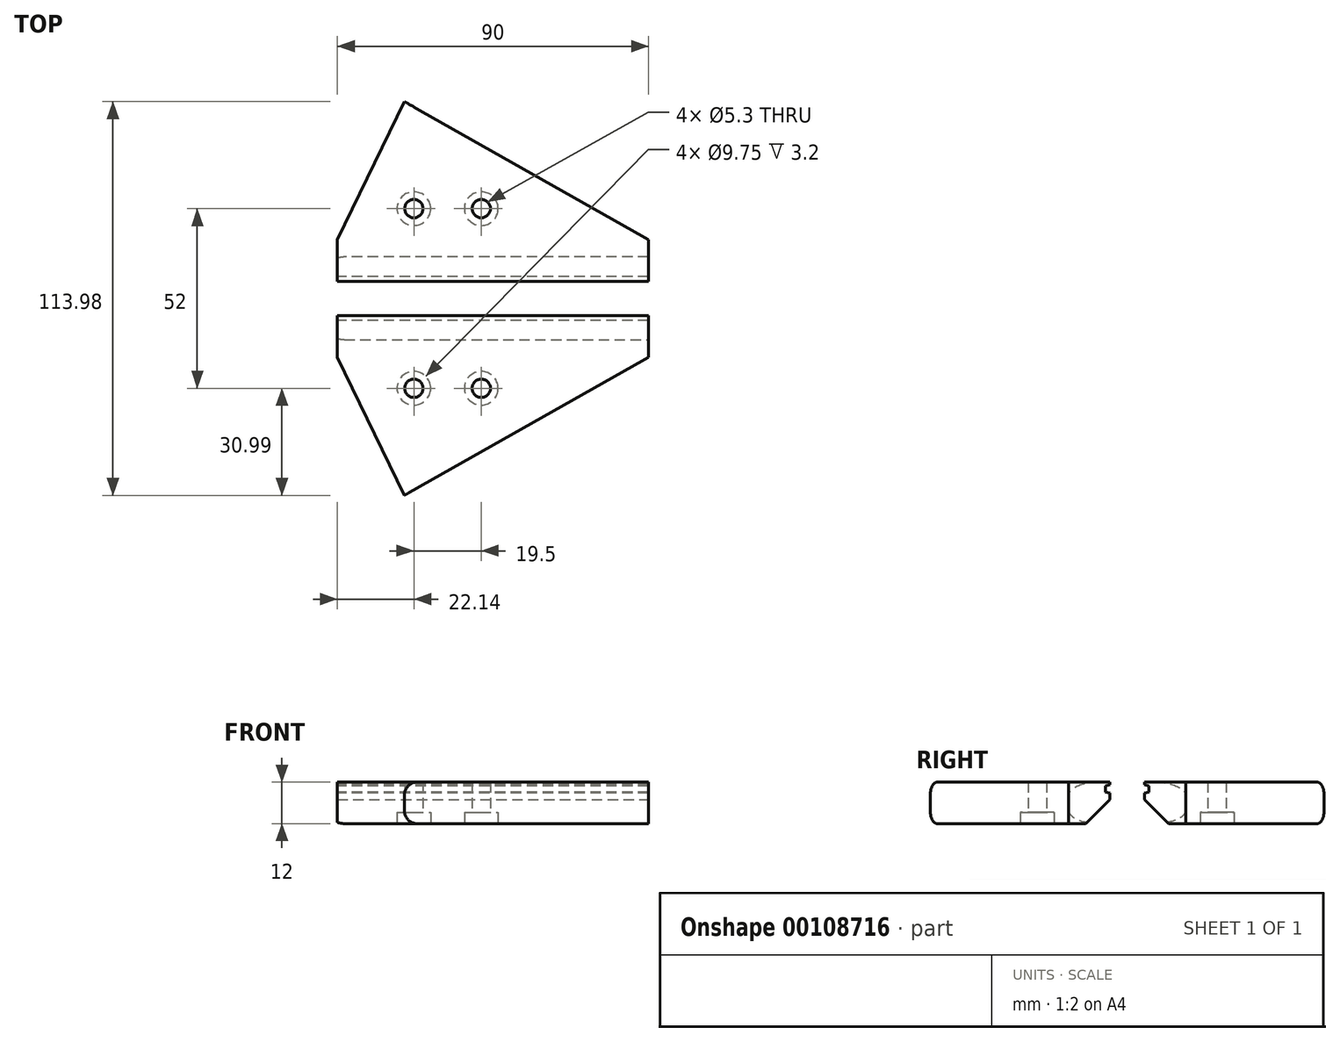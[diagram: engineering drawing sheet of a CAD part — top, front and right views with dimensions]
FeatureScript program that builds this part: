
annotation { "Feature Type Name" : "Feature", "Feature Type Description" : "" }
export const myFeature = defineFeature(function(context is Context, id is Id, definition is map)
    precondition{}
    {
        {
            var Q0;
            Q0=qCreatedBy(makeId("Top.planeOp"),FACE);
            var sketch = newSketch(context, id + "F0", { "sketchPlane" : qUnion([Q0])});
            skCircle(sketch, "E0", {"center": v(-9.75, -26) * mm, "radius": 4.75 * mm});
            skCircle(sketch, "E1", {"center": v(9.75, -26) * mm, "radius": 4.75 * mm});
            skCircle(sketch, "E2", {"center": v(-9.75, 26) * mm, "radius": 4.75 * mm});
            skCircle(sketch, "E3", {"center": v(9.75, 26) * mm, "radius": 4.75 * mm});
            skLineSegment(sketch, "E4", {"start": v(-9.75, 26) * mm, "end": v(9.75, 26) * mm, "construction": true});
            skPoint(sketch, "E5", {"position": v(0, 26) * mm});
            skLineSegment(sketch, "E6.bottom", {"start": v(19.1, 13.2) * mm, "end": v(-19.1, 13.2) * mm, "construction": true});
            skLineSegment(sketch, "E6.top", {"start": v(19.1, 38.8) * mm, "end": v(-19.1, 38.8) * mm, "construction": true});
            skLineSegment(sketch, "E6.left", {"start": v(19.1, 13.2) * mm, "end": v(19.1, 38.8) * mm, "construction": true});
            skLineSegment(sketch, "E6.right", {"start": v(-19.1, 13.2) * mm, "end": v(-19.1, 38.8) * mm, "construction": true});
            skLineSegment(sketch, "E7", {"start": v(-9.75, -26) * mm, "end": v(9.75, -26) * mm, "construction": true});
            skLineSegment(sketch, "E8", {"start": v(0, 26) * mm, "end": v(0, -26) * mm, "construction": true});
            skPoint(sketch, "E9", {"position": v(0, 0) * mm});
            skLineSegment(sketch, "E10.bottom", {"start": v(19.1, -38.8) * mm, "end": v(-19.1, -38.8) * mm, "construction": true});
            skLineSegment(sketch, "E10.top", {"start": v(19.1, -13.2) * mm, "end": v(-19.1, -13.2) * mm, "construction": true});
            skLineSegment(sketch, "E10.left", {"start": v(19.1, -38.8) * mm, "end": v(19.1, -13.2) * mm, "construction": true});
            skLineSegment(sketch, "E10.right", {"start": v(-19.1, -38.8) * mm, "end": v(-19.1, -13.2) * mm, "construction": true});
            skPoint(sketch, "E10.middle", {"position": v(0, -26) * mm});
            skSolve(sketch);
        }
        {
            var Q0;
            Q0=qCreatedBy(makeId("Top.planeOp"),FACE);
            var sketch = newSketch(context, id + "F1", { "sketchPlane" : qUnion([Q0])});
            skLineSegment(sketch, "E11", {"start": v(-31.9, 5) * mm, "end": v(58.1, 5) * mm});
            skLineSegment(sketch, "E12", {"start": v(-31.9, 5) * mm, "end": v(-31.9, 17) * mm});
            skLineSegment(sketch, "E13", {"start": v(58.1, 5) * mm, "end": v(58.1, 17) * mm});
            skLineSegment(sketch, "E14", {"start": v(58.1, 17) * mm, "end": v(-12.5, 57) * mm});
            skLineSegment(sketch, "E15", {"start": v(-31.9, 17) * mm, "end": v(-12.5, 57) * mm});
            skPoint(sketch, "E16", {"position": v(-9.75, 26) * mm});
            skPoint(sketch, "E17", {"position": v(9.75, 26) * mm});
            skLineSegment(sketch, "E18", {"start": v(-12.5, 57) * mm, "end": v(-47.57, 76.85) * mm, "construction": true});
            skLineSegment(sketch, "E19", {"start": v(-9.75, 26) * mm, "end": v(-24.15, 32.98) * mm, "construction": true});
            skLineSegment(sketch, "E20", {"start": v(9.75, 26) * mm, "end": v(17.64, 39.92) * mm, "construction": true});
            skLineSegment(sketch, "E21.MirrorCS", {"start": v(58.1, -17) * mm, "end": v(-12.5, -57) * mm, "construction": true});
            skLineSegment(sketch, "E22.MirrorCS", {"start": v(-31.9, -17) * mm, "end": v(-12.5, -57) * mm, "construction": true});
            skLineSegment(sketch, "E23.MirrorCS", {"start": v(58.1, -5) * mm, "end": v(58.1, -17) * mm});
            skLineSegment(sketch, "E24.MirrorCS", {"start": v(-31.9, -5) * mm, "end": v(-31.9, -17) * mm});
            skLineSegment(sketch, "E25.MirrorCS", {"start": v(58.1, -17) * mm, "end": v(-12.5, -57) * mm});
            skLineSegment(sketch, "E26.MirrorCS", {"start": v(-9.75, -26) * mm, "end": v(-24.15, -32.98) * mm, "construction": true});
            skPoint(sketch, "E27.MirrorP", {"position": v(-9.75, -26) * mm});
            skLineSegment(sketch, "E28.MirrorCS", {"start": v(9.75, -26) * mm, "end": v(17.64, -39.92) * mm, "construction": true});
            skPoint(sketch, "E29.MirrorP", {"position": v(9.75, -26) * mm});
            skLineSegment(sketch, "E30.MirrorCS", {"start": v(-31.9, -5) * mm, "end": v(58.1, -5) * mm});
            skLineSegment(sketch, "E31.MirrorCS", {"start": v(-31.9, -17) * mm, "end": v(-12.5, -57) * mm});
            skLineSegment(sketch, "E32.MirrorCS", {"start": v(58.1, 17) * mm, "end": v(-12.5, 57) * mm, "construction": true});
            skLineSegment(sketch, "E33.MirrorCS", {"start": v(-31.9, 17) * mm, "end": v(-12.5, 57) * mm, "construction": true});
            skSolve(sketch);
        }
        {
            var Q0;
            Q0=makeQuery(id+"F1.imprint","IMPRINT",FACE,{"disambiguationData":[TD([[makeQuery(id+"F1.imprint","IMPRINT",EDGE,{"derivedFrom":sQuery(id+"F1.wireOp",EDGE,"E11")}),1.0]])]});
            var Q1;
            Q1=makeQuery(id+"F1.imprint","IMPRINT",FACE,{"disambiguationData":[TD([[makeQuery(id+"F1.imprint","IMPRINT",EDGE,{"derivedFrom":sQuery(id+"F1.wireOp",EDGE,"f0b5c845-2ff2-45c4-aac1-717edb82d91d0.MirrorCS")}),1.0]])]});
            var Q2;
            Q2=makeQuery(id+"F1.imprint","IMPRINT",FACE,{"disambiguationData":[TD([[makeQuery(id+"F1.imprint","IMPRINT",EDGE,{"derivedFrom":sQuery(id+"F1.wireOp",EDGE,"E23.MirrorCS")}),-1.0]])]});
            extrude(context, id + "F2", {"entities" : qUnion([Q0, Q1, Q2]), "depth" : 12 * mm});
        }
        {
            var Q0;
            Q0=sQuery(id+"F0.wireOp",VERTEX,"E2.center");
            var Q1;
            Q1=sQuery(id+"F0.wireOp",VERTEX,"E3.center");
            var Q2;
            Q2=sQuery(id+"F0.wireOp",VERTEX,"E0.center");
            var Q3;
            Q3=sQuery(id+"F0.wireOp",VERTEX,"E1.center");
            var Q4;
            Q4=makeQuery(id+"F2.opExtrude","SWEPT_BODY",BODY,{"disambiguationData":[OSD([sQuery(id+"F1.wireOp",EDGE,"E11"),sQuery(id+"F1.wireOp",EDGE,"E12"),sQuery(id+"F1.wireOp",EDGE,"E13"),sQuery(id+"F1.wireOp",EDGE,"E14"),sQuery(id+"F1.wireOp",EDGE,"E15"),sQuery(id+"F1.wireOp",EDGE,"TzhvLS3T-Hups-Q3Qz-4XNe-3sz2j3HgjUnV")])]});
            var Q5;
            Q5=makeQuery(id+"F2.opExtrude","SWEPT_BODY",BODY,{"disambiguationData":[OSD([sQuery(id+"F1.wireOp",EDGE,"E23.MirrorCS"),sQuery(id+"F1.wireOp",EDGE,"E24.MirrorCS"),sQuery(id+"F1.wireOp",EDGE,"E25.MirrorCS"),sQuery(id+"F1.wireOp",EDGE,"E30.MirrorCS"),sQuery(id+"F1.wireOp",EDGE,"E31.MirrorCS")])]});
            hole(context, id + "F3", {"style" : HoleStyle.C_BORE, "endStyle" : HoleEndStyle.THROUGH, "oppositeDirection" : true, "holeDiameter" : 5.3 * mm, "cBoreDiameter" : 9.75 * mm, "cBoreDepth" : 3.2 * mm, "startFromSketch" : true, "locations" : qUnion([Q0, Q1, Q2, Q3]), "scope" : qUnion([Q4, Q5]), "isTappedThrough" : true});
        }
        {
            var Q0;
            Q0=qCreatedBy(makeId("Right.planeOp"),FACE);
            var sketch = newSketch(context, id + "F4", { "sketchPlane" : qUnion([Q0])});
            skLineSegment(sketch, "E34", {"start": v(6.3, 10.9) * mm, "end": v(6.3, 9.1) * mm});
            skPoint(sketch, "E35", {"position": v(5, 11.2) * mm});
            skLineSegment(sketch, "E36", {"start": v(5, 11.2) * mm, "end": v(6.3, 10.9) * mm});
            skLineSegment(sketch, "E37", {"start": v(6.3, 9.1) * mm, "end": v(5, 8.8) * mm});
            skLineSegment(sketch, "E38", {"start": v(5, 11.2) * mm, "end": v(5, 8.8) * mm});
            skLineSegment(sketch, "E39.MirrorCS", {"start": v(-6.3, 9.1) * mm, "end": v(-5, 8.8) * mm});
            skLineSegment(sketch, "E40.MirrorCS", {"start": v(-5, 11.2) * mm, "end": v(-6.3, 10.9) * mm});
            skLineSegment(sketch, "E41.MirrorCS", {"start": v(-5, 11.2) * mm, "end": v(-5, 8.8) * mm});
            skLineSegment(sketch, "E42.MirrorCS", {"start": v(-6.3, 10.9) * mm, "end": v(-6.3, 9.1) * mm});
            skPoint(sketch, "E43.MirrorP", {"position": v(-5, 11.2) * mm});
            skSolve(sketch);
        }
        {
            var Q0;
            Q0=makeQuery(id+"F4.imprint","IMPRINT",FACE,{"disambiguationData":[TD([[makeQuery(id+"F4.imprint","IMPRINT",EDGE,{"derivedFrom":sQuery(id+"F4.wireOp",EDGE,"E39.MirrorCS")}),1.0]])]});
            var Q1;
            Q1=makeQuery(id+"F4.imprint","IMPRINT",FACE,{"disambiguationData":[TD([[makeQuery(id+"F4.imprint","IMPRINT",EDGE,{"derivedFrom":sQuery(id+"F4.wireOp",EDGE,"E34")}),-1.0]])]});
            extrude(context, id + "F5", {"entities" : qUnion([Q0, Q1]), "operationType" : NewBodyOperationType.REMOVE, "endBound" : BoundingType.THROUGH_ALL, "depth" : 25 * mm, "hasSecondDirection" : true, "secondDirectionBound" : SecondDirectionBoundingType.THROUGH_ALL, "secondDirectionOppositeDirection" : true, "secondDirectionDepth" : 25 * mm});
        }
        {
            var Q0;
            Q0=makeQuery(id+"F2.opExtrude","CAP_EDGE",EDGE,{"disambiguationData":[OSD([sQuery(id+"F1.wireOp",EDGE,"E15")])],"isStart":false});
            var Q1;
            Q1=makeQuery(id+"F2.opExtrude","CAP_EDGE",EDGE,{"disambiguationData":[OSD([sQuery(id+"F1.wireOp",EDGE,"E15")])],"isStart":true});
            var Q2;
            Q2=makeQuery(id+"F2.opExtrude","CAP_EDGE",EDGE,{"disambiguationData":[OSD([sQuery(id+"F1.wireOp",EDGE,"E31.MirrorCS")])],"isStart":true});
            var Q3;
            Q3=makeQuery(id+"F2.opExtrude","CAP_EDGE",EDGE,{"disambiguationData":[OSD([sQuery(id+"F1.wireOp",EDGE,"E31.MirrorCS")])],"isStart":false});
            fillet(context, id + "F6", {"entities" : qUnion([Q0, Q1, Q2, Q3]), "radius" : 4 * mm, "tangentPropagation" : true, "allowEdgeOverflow" : false});
        }
        {
            var Q0;
            Q0=makeQuery(id+"F2.opExtrude","CAP_EDGE",EDGE,{"disambiguationData":[OSD([sQuery(id+"F1.wireOp",EDGE,"E30.MirrorCS")])],"isStart":true});
            var Q1;
            Q1=makeQuery(id+"F2.opExtrude","CAP_EDGE",EDGE,{"disambiguationData":[OSD([sQuery(id+"F1.wireOp",EDGE,"E11")])],"isStart":true});
            chamfer(context, id + "F7", {"entities" : qUnion([Q0, Q1]), "width" : 7 * mm, "tangentPropagation" : true});
        }
    });
